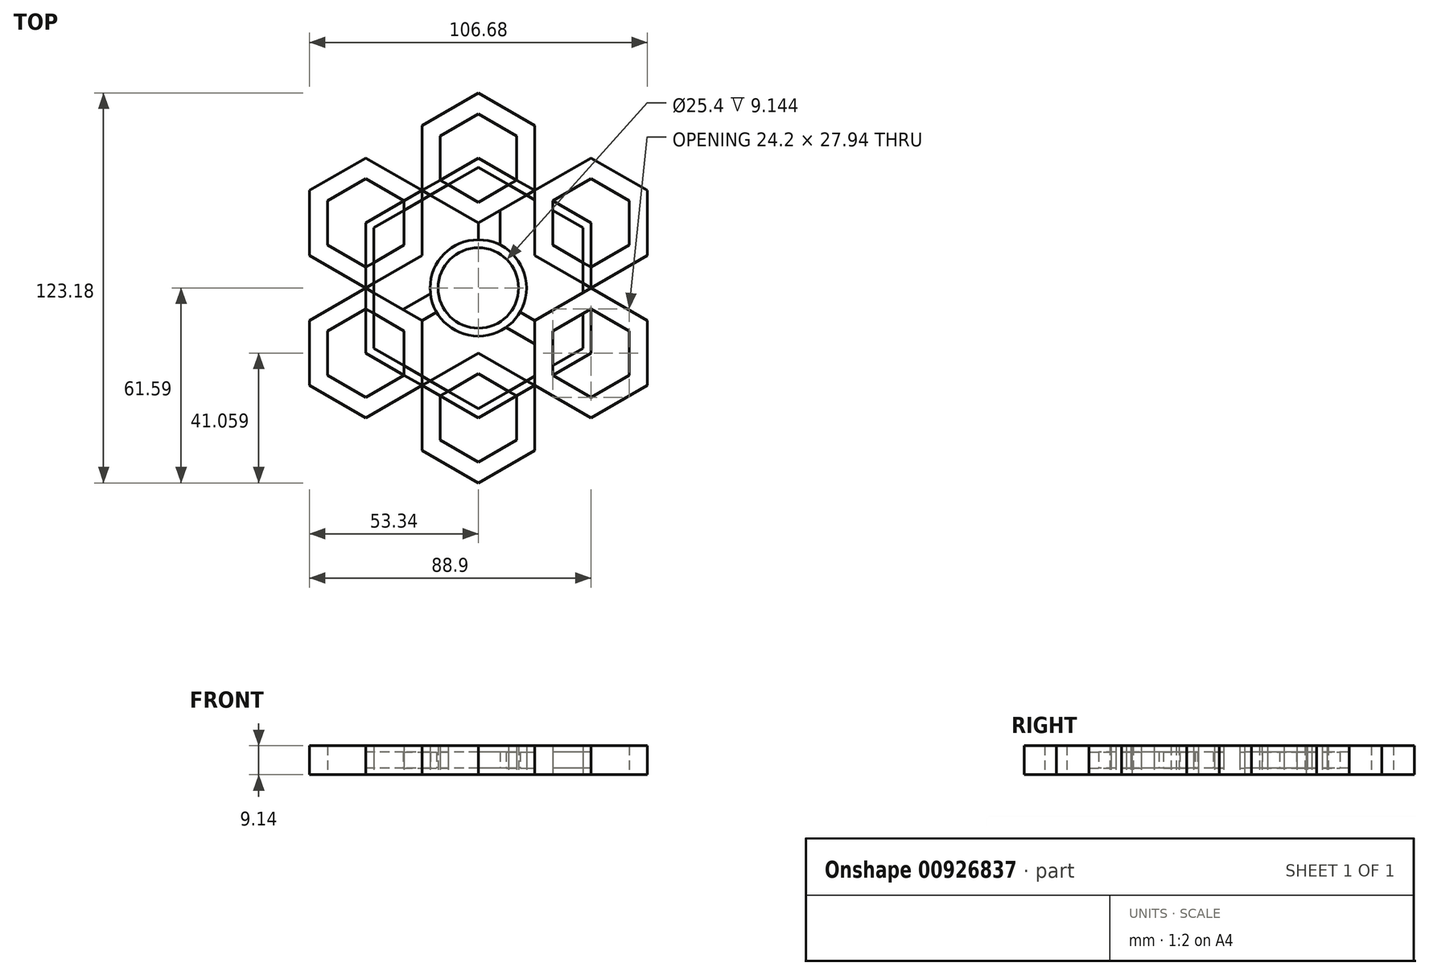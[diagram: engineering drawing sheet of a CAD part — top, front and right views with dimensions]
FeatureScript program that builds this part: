
annotation { "Feature Type Name" : "Feature", "Feature Type Description" : "" }
export const myFeature = defineFeature(function(context is Context, id is Id, definition is map)
    precondition{}
    {
        {
            var Q0;
            Q0=qCreatedBy(makeId("Top.planeOp"),FACE);
            var sketch = newSketch(context, id + "F0", { "sketchPlane" : qUnion([Q0])});
            skCircle(sketch, "E0", {"center": v(0, 0) * mm, "radius": 12.7 * mm});
            skCircle(sketch, "E1.cCircle", {"center": v(0, 0) * mm, "radius": 35.56 * mm, "construction": true});
            skLineSegment(sketch, "E1.0", {"start": v(35.56, 20.53) * mm, "end": v(35.56, -20.53) * mm});
            skLineSegment(sketch, "E1.1", {"start": v(35.56, -20.53) * mm, "end": v(0, -41.06) * mm});
            skLineSegment(sketch, "E1.2", {"start": v(0, -41.06) * mm, "end": v(-35.56, -20.53) * mm});
            skLineSegment(sketch, "E1.3", {"start": v(-35.56, -20.53) * mm, "end": v(-35.56, 20.53) * mm});
            skLineSegment(sketch, "E1.4", {"start": v(-35.56, 20.53) * mm, "end": v(0, 41.06) * mm});
            skLineSegment(sketch, "E1.5", {"start": v(0, 41.06) * mm, "end": v(35.56, 20.53) * mm});
            skPoint(sketch, "E1.0.midPoint", {"position": v(35.56, 0) * mm});
            skCircle(sketch, "E2.cCircle", {"center": v(35.56, 20.53) * mm, "radius": 20.53 * mm, "construction": true});
            skLineSegment(sketch, "E2.0", {"start": v(35.56, 0) * mm, "end": v(17.78, 10.27) * mm});
            skLineSegment(sketch, "E2.1", {"start": v(17.78, 10.27) * mm, "end": v(17.78, 30.8) * mm});
            skLineSegment(sketch, "E2.2", {"start": v(17.78, 30.8) * mm, "end": v(35.56, 41.06) * mm});
            skLineSegment(sketch, "E2.3", {"start": v(35.56, 41.06) * mm, "end": v(53.34, 30.8) * mm});
            skLineSegment(sketch, "E2.4", {"start": v(53.34, 30.8) * mm, "end": v(53.34, 10.27) * mm});
            skLineSegment(sketch, "E2.5", {"start": v(53.34, 10.27) * mm, "end": v(35.56, 0) * mm});
            skCircle(sketch, "E3.cCircle", {"center": v(0, 41.06) * mm, "radius": 20.53 * mm, "construction": true});
            skLineSegment(sketch, "E3.0", {"start": v(17.78, 30.8) * mm, "end": v(0, 20.53) * mm});
            skLineSegment(sketch, "E3.1", {"start": v(0, 20.53) * mm, "end": v(-17.78, 30.8) * mm});
            skLineSegment(sketch, "E3.2", {"start": v(-17.78, 30.8) * mm, "end": v(-17.78, 51.33) * mm});
            skLineSegment(sketch, "E3.3", {"start": v(-17.78, 51.33) * mm, "end": v(0, 61.6) * mm});
            skLineSegment(sketch, "E3.4", {"start": v(0, 61.6) * mm, "end": v(17.78, 51.33) * mm});
            skLineSegment(sketch, "E3.5", {"start": v(17.78, 51.33) * mm, "end": v(17.78, 30.8) * mm});
            skCircle(sketch, "E4.cCircle", {"center": v(-35.56, 20.53) * mm, "radius": 20.53 * mm, "construction": true});
            skLineSegment(sketch, "E4.0", {"start": v(-17.78, 30.8) * mm, "end": v(-17.78, 10.27) * mm});
            skLineSegment(sketch, "E4.1", {"start": v(-17.78, 10.27) * mm, "end": v(-35.56, 0) * mm});
            skLineSegment(sketch, "E4.2", {"start": v(-35.56, 0) * mm, "end": v(-53.34, 10.27) * mm});
            skLineSegment(sketch, "E4.3", {"start": v(-53.34, 10.27) * mm, "end": v(-53.34, 30.8) * mm});
            skLineSegment(sketch, "E4.4", {"start": v(-53.34, 30.8) * mm, "end": v(-35.56, 41.06) * mm});
            skLineSegment(sketch, "E4.5", {"start": v(-35.56, 41.06) * mm, "end": v(-17.78, 30.8) * mm});
            skCircle(sketch, "E5.cCircle", {"center": v(-35.56, -20.53) * mm, "radius": 20.53 * mm, "construction": true});
            skLineSegment(sketch, "E5.0", {"start": v(-35.56, 0) * mm, "end": v(-17.78, -10.27) * mm});
            skLineSegment(sketch, "E5.1", {"start": v(-17.78, -10.27) * mm, "end": v(-17.78, -30.8) * mm});
            skLineSegment(sketch, "E5.2", {"start": v(-17.78, -30.8) * mm, "end": v(-35.56, -41.06) * mm});
            skLineSegment(sketch, "E5.3", {"start": v(-35.56, -41.06) * mm, "end": v(-53.34, -30.8) * mm});
            skLineSegment(sketch, "E5.4", {"start": v(-53.34, -30.8) * mm, "end": v(-53.34, -10.27) * mm});
            skLineSegment(sketch, "E5.5", {"start": v(-53.34, -10.27) * mm, "end": v(-35.56, 0) * mm});
            skCircle(sketch, "E6.cCircle", {"center": v(0, -41.06) * mm, "radius": 20.53 * mm, "construction": true});
            skLineSegment(sketch, "E6.0", {"start": v(-17.78, -30.8) * mm, "end": v(0, -20.53) * mm});
            skLineSegment(sketch, "E6.1", {"start": v(0, -20.53) * mm, "end": v(17.78, -30.8) * mm});
            skLineSegment(sketch, "E6.2", {"start": v(17.78, -30.8) * mm, "end": v(17.78, -51.33) * mm});
            skLineSegment(sketch, "E6.3", {"start": v(17.78, -51.33) * mm, "end": v(0, -61.6) * mm});
            skLineSegment(sketch, "E6.4", {"start": v(0, -61.6) * mm, "end": v(-17.78, -51.33) * mm});
            skLineSegment(sketch, "E6.5", {"start": v(-17.78, -51.33) * mm, "end": v(-17.78, -30.8) * mm});
            skCircle(sketch, "E7.cCircle", {"center": v(35.56, -20.53) * mm, "radius": 20.53 * mm, "construction": true});
            skLineSegment(sketch, "E7.0", {"start": v(35.56, 0) * mm, "end": v(53.34, -10.27) * mm});
            skLineSegment(sketch, "E7.1", {"start": v(53.34, -10.27) * mm, "end": v(53.34, -30.8) * mm});
            skLineSegment(sketch, "E7.2", {"start": v(53.34, -30.8) * mm, "end": v(35.56, -41.06) * mm});
            skLineSegment(sketch, "E7.3", {"start": v(35.56, -41.06) * mm, "end": v(17.78, -30.8) * mm});
            skLineSegment(sketch, "E7.4", {"start": v(17.78, -30.8) * mm, "end": v(17.78, -10.27) * mm});
            skLineSegment(sketch, "E7.5", {"start": v(17.78, -10.27) * mm, "end": v(35.56, 0) * mm});
            skCircle(sketch, "E8.cCircle", {"center": v(-35.56, 20.53) * mm, "radius": 13.97 * mm, "construction": true});
            skLineSegment(sketch, "E8.0", {"start": v(-35.56, 6.56) * mm, "end": v(-47.66, 13.55) * mm});
            skLineSegment(sketch, "E8.1", {"start": v(-47.66, 13.55) * mm, "end": v(-47.66, 27.52) * mm});
            skLineSegment(sketch, "E8.2", {"start": v(-47.66, 27.52) * mm, "end": v(-35.56, 34.5) * mm});
            skLineSegment(sketch, "E8.3", {"start": v(-35.56, 34.5) * mm, "end": v(-23.46, 27.52) * mm});
            skLineSegment(sketch, "E8.4", {"start": v(-23.46, 27.52) * mm, "end": v(-23.46, 13.55) * mm});
            skLineSegment(sketch, "E8.5", {"start": v(-23.46, 13.55) * mm, "end": v(-35.56, 6.56) * mm});
            skCircle(sketch, "E9.cCircle", {"center": v(0, 41.06) * mm, "radius": 13.97 * mm, "construction": true});
            skLineSegment(sketch, "E9.0", {"start": v(0, 55.03) * mm, "end": v(12.1, 48.05) * mm});
            skLineSegment(sketch, "E9.1", {"start": v(12.1, 48.05) * mm, "end": v(12.1, 34.08) * mm});
            skLineSegment(sketch, "E9.2", {"start": v(12.1, 34.08) * mm, "end": v(0, 27.1) * mm});
            skLineSegment(sketch, "E9.3", {"start": v(0, 27.1) * mm, "end": v(-12.1, 34.08) * mm});
            skLineSegment(sketch, "E9.4", {"start": v(-12.1, 34.08) * mm, "end": v(-12.1, 48.05) * mm});
            skLineSegment(sketch, "E9.5", {"start": v(-12.1, 48.05) * mm, "end": v(0, 55.03) * mm});
            skCircle(sketch, "E10.cCircle", {"center": v(35.56, 20.53) * mm, "radius": 13.97 * mm, "construction": true});
            skLineSegment(sketch, "E10.0", {"start": v(35.56, 6.56) * mm, "end": v(23.46, 13.55) * mm});
            skLineSegment(sketch, "E10.1", {"start": v(23.46, 13.55) * mm, "end": v(23.46, 27.52) * mm});
            skLineSegment(sketch, "E10.2", {"start": v(23.46, 27.52) * mm, "end": v(35.56, 34.5) * mm});
            skLineSegment(sketch, "E10.3", {"start": v(35.56, 34.5) * mm, "end": v(47.66, 27.52) * mm});
            skLineSegment(sketch, "E10.4", {"start": v(47.66, 27.52) * mm, "end": v(47.66, 13.55) * mm});
            skLineSegment(sketch, "E10.5", {"start": v(47.66, 13.55) * mm, "end": v(35.56, 6.56) * mm});
            skCircle(sketch, "E11.cCircle", {"center": v(35.56, -20.53) * mm, "radius": 13.97 * mm, "construction": true});
            skLineSegment(sketch, "E11.0", {"start": v(35.56, -34.5) * mm, "end": v(23.46, -27.52) * mm});
            skLineSegment(sketch, "E11.1", {"start": v(23.46, -27.52) * mm, "end": v(23.46, -13.55) * mm});
            skLineSegment(sketch, "E11.2", {"start": v(23.46, -13.55) * mm, "end": v(35.56, -6.56) * mm});
            skLineSegment(sketch, "E11.3", {"start": v(35.56, -6.56) * mm, "end": v(47.66, -13.55) * mm});
            skLineSegment(sketch, "E11.4", {"start": v(47.66, -13.55) * mm, "end": v(47.66, -27.52) * mm});
            skLineSegment(sketch, "E11.5", {"start": v(47.66, -27.52) * mm, "end": v(35.56, -34.5) * mm});
            skCircle(sketch, "E12.cCircle", {"center": v(0, -41.06) * mm, "radius": 12.1 * mm, "construction": true});
            skLineSegment(sketch, "E12.0", {"start": v(0, -55.03) * mm, "end": v(-12.1, -48.05) * mm});
            skLineSegment(sketch, "E12.1", {"start": v(-12.1, -48.05) * mm, "end": v(-12.1, -34.08) * mm});
            skLineSegment(sketch, "E12.2", {"start": v(-12.1, -34.08) * mm, "end": v(0, -27.1) * mm});
            skLineSegment(sketch, "E12.3", {"start": v(0, -27.1) * mm, "end": v(12.1, -34.08) * mm});
            skLineSegment(sketch, "E12.4", {"start": v(12.1, -34.08) * mm, "end": v(12.1, -48.05) * mm});
            skLineSegment(sketch, "E12.5", {"start": v(12.1, -48.05) * mm, "end": v(0, -55.03) * mm});
            skPoint(sketch, "E12.0.midPoint", {"position": v(-6.05, -51.54) * mm});
            skCircle(sketch, "E13.cCircle", {"center": v(-35.56, -20.53) * mm, "radius": 13.97 * mm, "construction": true});
            skLineSegment(sketch, "E13.0", {"start": v(-35.56, -6.56) * mm, "end": v(-23.46, -13.55) * mm});
            skLineSegment(sketch, "E13.1", {"start": v(-23.46, -13.55) * mm, "end": v(-23.46, -27.52) * mm});
            skLineSegment(sketch, "E13.2", {"start": v(-23.46, -27.52) * mm, "end": v(-35.56, -34.5) * mm});
            skLineSegment(sketch, "E13.3", {"start": v(-35.56, -34.5) * mm, "end": v(-47.66, -27.52) * mm});
            skLineSegment(sketch, "E13.4", {"start": v(-47.66, -27.52) * mm, "end": v(-47.66, -13.55) * mm});
            skLineSegment(sketch, "E13.5", {"start": v(-47.66, -13.55) * mm, "end": v(-35.56, -6.56) * mm});
            skLineSegment(sketch, "E14", {"start": v(-17.78, -10.27) * mm, "end": v(0, 0) * mm});
            skLineSegment(sketch, "E15", {"start": v(0, 20.53) * mm, "end": v(0, 0) * mm});
            skLineSegment(sketch, "E16", {"start": v(0, 0) * mm, "end": v(17.78, -10.27) * mm});
            skLineSegment(sketch, "E17", {"start": v(0, 0) * mm, "end": v(0, -7.37) * mm});
            skLineSegment(sketch, "E18", {"start": v(0, -7.37) * mm, "end": v(0, 0) * mm});
            skLineSegment(sketch, "E19", {"start": v(0, 0) * mm, "end": v(6.87, 3.97) * mm});
            skLineSegment(sketch, "E20", {"start": v(0, 0) * mm, "end": v(-6, 3.46) * mm});
            skLineSegment(sketch, "E21", {"start": v(-6, 3.46) * mm, "end": v(-23.77, -6.8) * mm});
            skLineSegment(sketch, "E22", {"start": v(6.87, 3.97) * mm, "end": v(6.87, 24.5) * mm});
            skLineSegment(sketch, "E23", {"start": v(0, -7.37) * mm, "end": v(17.78, -17.63) * mm});
            skCircle(sketch, "E24", {"center": v(0, 0) * mm, "radius": 15.24 * mm});
            skCircle(sketch, "E25.cCircle", {"center": v(0, 0) * mm, "radius": 38.1 * mm, "construction": true});
            skLineSegment(sketch, "E25.0", {"start": v(0, 38.1) * mm, "end": v(33, 19.05) * mm});
            skLineSegment(sketch, "E25.1", {"start": v(33, 19.05) * mm, "end": v(33, -19.05) * mm});
            skLineSegment(sketch, "E25.2", {"start": v(33, -19.05) * mm, "end": v(0, -38.1) * mm});
            skLineSegment(sketch, "E25.3", {"start": v(0, -38.1) * mm, "end": v(-33, -19.05) * mm});
            skLineSegment(sketch, "E25.4", {"start": v(-33, -19.05) * mm, "end": v(-33, 19.05) * mm});
            skLineSegment(sketch, "E25.5", {"start": v(-33, 19.05) * mm, "end": v(0, 38.1) * mm});
            skSolve(sketch);
        }
        {
            var Q0;
            {var subQ0=sQuery(id+"F0.wireOp",EDGE,"E4.2");Q0=makeQuery(id+"F0.imprint","IMPRINT",FACE,{"disambiguationData":[TD([[makeQuery(id+"F0.imprint","IMPRINT",EDGE,{"derivedFrom":subQ0}),-1.0]])]});}
            var Q1;
            {var subQ0=sQuery(id+"F0.wireOp",EDGE,"E3.2");Q1=makeQuery(id+"F0.imprint","IMPRINT",FACE,{"disambiguationData":[TD([[makeQuery(id+"F0.imprint","IMPRINT",EDGE,{"derivedFrom":subQ0}),-1.0]])]});}
            var Q2;
            {var subQ1=sQuery(id+"F0.wireOp",EDGE,"E2.2");Q2=makeQuery(id+"F0.imprint","IMPRINT",FACE,{"disambiguationData":[TD([[makeQuery(id+"F0.imprint","IMPRINT",EDGE,{"derivedFrom":subQ1}),-1.0]])]});}
            var Q3;
            {var subQ0=sQuery(id+"F0.wireOp",EDGE,"E7.0");Q3=makeQuery(id+"F0.imprint","IMPRINT",FACE,{"disambiguationData":[TD([[makeQuery(id+"F0.imprint","IMPRINT",EDGE,{"derivedFrom":subQ0}),-1.0]])]});}
            var Q4;
            {var subQ0=sQuery(id+"F0.wireOp",EDGE,"E6.2");Q4=makeQuery(id+"F0.imprint","IMPRINT",FACE,{"disambiguationData":[TD([[makeQuery(id+"F0.imprint","IMPRINT",EDGE,{"derivedFrom":subQ0}),-1.0]])]});}
            var Q5;
            {var subQ0=sQuery(id+"F0.wireOp",EDGE,"E5.2");Q5=makeQuery(id+"F0.imprint","IMPRINT",FACE,{"disambiguationData":[TD([[makeQuery(id+"F0.imprint","IMPRINT",EDGE,{"derivedFrom":subQ0}),-1.0]])]});}
            var Q6;
            {var subQ7=sQuery(id+"F0.wireOp",EDGE,"E4.1");var subQ8=sQuery(id+"F0.wireOp",EDGE,"E4.0");var subQ9=makeQuery(id+"F0.imprint","INTERSECT",VERTEX,{"derivedFrom":[subQ8,subQ7]});Q6=makeQuery(id+"F0.imprint","IMPRINT",FACE,{"disambiguationData":[TD([[makeQuery(id+"F0.imprint","IMPRINT",EDGE,{"disambiguationData":[TD([[subQ9,1.0]])],"derivedFrom":subQ8}),-1.0]])]});}
            var Q7;
            {var subQ6=sQuery(id+"F0.wireOp",EDGE,"E3.0");var subQ11=makeQuery(id+"F0.imprint","INTERSECT",VERTEX,{"derivedFrom":[subQ6,sQuery(id+"F0.wireOp",EDGE,"E22")]});Q7=makeQuery(id+"F0.imprint","IMPRINT",FACE,{"disambiguationData":[TD([[makeQuery(id+"F0.imprint","IMPRINT",EDGE,{"disambiguationData":[TD([[subQ11,1.0]])],"derivedFrom":subQ6}),-1.0]])]});}
            var Q8;
            {var subQ7=sQuery(id+"F0.wireOp",EDGE,"E2.1");var subQ8=sQuery(id+"F0.wireOp",EDGE,"E2.0");var subQ9=makeQuery(id+"F0.imprint","INTERSECT",VERTEX,{"derivedFrom":[subQ8,subQ7]});Q8=makeQuery(id+"F0.imprint","IMPRINT",FACE,{"disambiguationData":[TD([[makeQuery(id+"F0.imprint","IMPRINT",EDGE,{"disambiguationData":[TD([[subQ9,1.0]])],"derivedFrom":subQ8}),-1.0]])]});}
            var Q9;
            {var subQ1=sQuery(id+"F0.wireOp",EDGE,"E7.4");var subQ9=makeQuery(id+"F0.imprint","INTERSECT",VERTEX,{"derivedFrom":[subQ1,sQuery(id+"F0.wireOp",EDGE,"E23")]});Q9=makeQuery(id+"F0.imprint","IMPRINT",FACE,{"disambiguationData":[TD([[makeQuery(id+"F0.imprint","IMPRINT",EDGE,{"disambiguationData":[TD([[subQ9,1.0]])],"derivedFrom":subQ1}),-1.0]])]});}
            var Q10;
            {var subQ6=sQuery(id+"F0.wireOp",EDGE,"E6.0");var subQ9=sQuery(id+"F0.wireOp",EDGE,"E6.1");var subQ10=makeQuery(id+"F0.imprint","INTERSECT",VERTEX,{"derivedFrom":[subQ6,subQ9]});Q10=makeQuery(id+"F0.imprint","IMPRINT",FACE,{"disambiguationData":[TD([[makeQuery(id+"F0.imprint","IMPRINT",EDGE,{"disambiguationData":[TD([[subQ10,1.0]])],"derivedFrom":subQ6}),-1.0]])]});}
            var Q11;
            {var subQ1=sQuery(id+"F0.wireOp",EDGE,"E5.0");var subQ10=makeQuery(id+"F0.imprint","INTERSECT",VERTEX,{"derivedFrom":[subQ1,sQuery(id+"F0.wireOp",EDGE,"E21")]});Q11=makeQuery(id+"F0.imprint","IMPRINT",FACE,{"disambiguationData":[TD([[makeQuery(id+"F0.imprint","IMPRINT",EDGE,{"disambiguationData":[TD([[subQ10,1.0]])],"derivedFrom":subQ1}),-1.0]])]});}
            var Q12;
            {var subQ0=sQuery(id+"F0.wireOp",EDGE,"E14");var subQ1=sQuery(id+"F0.wireOp",EDGE,"E0");var subQ2=makeQuery(id+"F0.imprint","INTERSECT",VERTEX,{"derivedFrom":[subQ1,subQ0]});Q12=makeQuery(id+"F0.imprint","IMPRINT",FACE,{"disambiguationData":[TD([[makeQuery(id+"F0.imprint","IMPRINT",EDGE,{"disambiguationData":[TD([[subQ2,-1.0]])],"derivedFrom":subQ1}),-1.0]])]});}
            var Q13;
            {var subQ0=sQuery(id+"F0.wireOp",EDGE,"E15");var subQ1=sQuery(id+"F0.wireOp",EDGE,"E0");var subQ2=makeQuery(id+"F0.imprint","INTERSECT",VERTEX,{"derivedFrom":[subQ1,subQ0]});Q13=makeQuery(id+"F0.imprint","IMPRINT",FACE,{"disambiguationData":[TD([[makeQuery(id+"F0.imprint","IMPRINT",EDGE,{"disambiguationData":[TD([[subQ2,-1.0]])],"derivedFrom":subQ1}),-1.0]])]});}
            var Q14;
            {var subQ0=sQuery(id+"F0.wireOp",EDGE,"E22");var subQ1=sQuery(id+"F0.wireOp",EDGE,"E0");var subQ2=makeQuery(id+"F0.imprint","INTERSECT",VERTEX,{"derivedFrom":[subQ1,subQ0]});Q14=makeQuery(id+"F0.imprint","IMPRINT",FACE,{"disambiguationData":[TD([[makeQuery(id+"F0.imprint","IMPRINT",EDGE,{"disambiguationData":[TD([[subQ2,1.0]])],"derivedFrom":subQ1}),-1.0]])]});}
            var Q15;
            {var subQ0=sQuery(id+"F0.wireOp",EDGE,"E23");var subQ1=sQuery(id+"F0.wireOp",EDGE,"E0");var subQ2=makeQuery(id+"F0.imprint","INTERSECT",VERTEX,{"derivedFrom":[subQ1,subQ0]});Q15=makeQuery(id+"F0.imprint","IMPRINT",FACE,{"disambiguationData":[TD([[makeQuery(id+"F0.imprint","IMPRINT",EDGE,{"disambiguationData":[TD([[subQ2,-1.0]])],"derivedFrom":subQ1}),-1.0]])]});}
            var Q16;
            {var subQ0=sQuery(id+"F0.wireOp",EDGE,"E15");var subQ1=sQuery(id+"F0.wireOp",EDGE,"E0");var subQ2=makeQuery(id+"F0.imprint","INTERSECT",VERTEX,{"derivedFrom":[subQ1,subQ0]});Q16=makeQuery(id+"F0.imprint","IMPRINT",FACE,{"disambiguationData":[TD([[makeQuery(id+"F0.imprint","IMPRINT",EDGE,{"disambiguationData":[TD([[subQ2,1.0]])],"derivedFrom":subQ1}),-1.0]])]});}
            var Q17;
            {var subQ0=sQuery(id+"F0.wireOp",EDGE,"E21");var subQ1=sQuery(id+"F0.wireOp",EDGE,"E0");var subQ2=makeQuery(id+"F0.imprint","INTERSECT",VERTEX,{"derivedFrom":[subQ1,subQ0]});Q17=makeQuery(id+"F0.imprint","IMPRINT",FACE,{"disambiguationData":[TD([[makeQuery(id+"F0.imprint","IMPRINT",EDGE,{"disambiguationData":[TD([[subQ2,-1.0]])],"derivedFrom":subQ1}),-1.0]])]});}
            extrude(context, id + "F1", {"entities" : qUnion([Q0, Q1, Q2, Q3, Q4, Q5, Q6, Q7, Q8, Q9, Q10, Q11, Q12, Q13, Q14, Q15, Q16, Q17]), "depth" : 4.57 * mm, "offsetDistance" : 25.4 * mm, "hasSecondDirection" : true, "secondDirectionOppositeDirection" : true, "secondDirectionDepth" : 4.57 * mm});
        }
        {
            var Q0;
            {var subQ1=sQuery(id+"F0.wireOp",EDGE,"E5.0");var subQ3=sQuery(id+"F0.wireOp",EDGE,"E21");var subQ4=makeQuery(id+"F0.imprint","INTERSECT",VERTEX,{"derivedFrom":[subQ1,subQ3]});Q0=makeQuery(id+"F0.imprint","IMPRINT",FACE,{"disambiguationData":[TD([[makeQuery(id+"F0.imprint","IMPRINT",EDGE,{"disambiguationData":[TD([[subQ4,1.0]])],"derivedFrom":subQ3}),1.0]])]});}
            var Q1;
            {var subQ3=sQuery(id+"F0.wireOp",EDGE,"E25.4");var subQ9=sQuery(id+"F0.wireOp",EDGE,"E25.5");var subQ11=makeQuery(id+"F0.imprint","INTERSECT",VERTEX,{"derivedFrom":[subQ3,subQ9]});Q1=makeQuery(id+"F0.imprint","IMPRINT",FACE,{"disambiguationData":[TD([[makeQuery(id+"F0.imprint","IMPRINT",EDGE,{"disambiguationData":[TD([[subQ11,1.0]])],"derivedFrom":subQ3}),1.0]])]});}
            var Q2;
            {var subQ1=sQuery(id+"F0.wireOp",EDGE,"E3.1");var subQ3=sQuery(id+"F0.wireOp",EDGE,"E25.5");var subQ4=makeQuery(id+"F0.imprint","INTERSECT",VERTEX,{"derivedFrom":[subQ1,subQ3]});Q2=makeQuery(id+"F0.imprint","IMPRINT",FACE,{"disambiguationData":[TD([[makeQuery(id+"F0.imprint","IMPRINT",EDGE,{"disambiguationData":[TD([[subQ4,1.0]])],"derivedFrom":subQ3}),1.0]])]});}
            var Q3;
            {var subQ3=sQuery(id+"F0.wireOp",EDGE,"E25.5");var subQ8=sQuery(id+"F0.wireOp",EDGE,"E25.0");var subQ11=makeQuery(id+"F0.imprint","INTERSECT",VERTEX,{"derivedFrom":[subQ8,subQ3]});Q3=makeQuery(id+"F0.imprint","IMPRINT",FACE,{"disambiguationData":[TD([[makeQuery(id+"F0.imprint","IMPRINT",EDGE,{"disambiguationData":[TD([[subQ11,-1.0]])],"derivedFrom":subQ8}),1.0]])]});}
            var Q4;
            {var subQ1=sQuery(id+"F0.wireOp",EDGE,"E2.1");var subQ3=sQuery(id+"F0.wireOp",EDGE,"E25.0");var subQ4=makeQuery(id+"F0.imprint","INTERSECT",VERTEX,{"derivedFrom":[subQ1,subQ3]});Q4=makeQuery(id+"F0.imprint","IMPRINT",FACE,{"disambiguationData":[TD([[makeQuery(id+"F0.imprint","IMPRINT",EDGE,{"disambiguationData":[TD([[subQ4,1.0]])],"derivedFrom":subQ3}),1.0]])]});}
            var Q5;
            {var subQ1=sQuery(id+"F0.wireOp",EDGE,"E2.0");var subQ3=sQuery(id+"F0.wireOp",EDGE,"E25.1");var subQ4=makeQuery(id+"F0.imprint","INTERSECT",VERTEX,{"derivedFrom":[subQ1,subQ3]});Q5=makeQuery(id+"F0.imprint","IMPRINT",FACE,{"disambiguationData":[TD([[makeQuery(id+"F0.imprint","IMPRINT",EDGE,{"disambiguationData":[TD([[subQ4,-1.0]])],"derivedFrom":subQ3}),1.0]])]});}
            var Q6;
            {var subQ1=sQuery(id+"F0.wireOp",EDGE,"E6.1");var subQ3=sQuery(id+"F0.wireOp",EDGE,"E25.2");var subQ4=makeQuery(id+"F0.imprint","INTERSECT",VERTEX,{"derivedFrom":[subQ1,subQ3]});Q6=makeQuery(id+"F0.imprint","IMPRINT",FACE,{"disambiguationData":[TD([[makeQuery(id+"F0.imprint","IMPRINT",EDGE,{"disambiguationData":[TD([[subQ4,1.0]])],"derivedFrom":subQ3}),1.0]])]});}
            var Q7;
            {var subQ1=sQuery(id+"F0.wireOp",EDGE,"E5.1");var subQ3=sQuery(id+"F0.wireOp",EDGE,"E25.3");var subQ4=makeQuery(id+"F0.imprint","INTERSECT",VERTEX,{"derivedFrom":[subQ1,subQ3]});Q7=makeQuery(id+"F0.imprint","IMPRINT",FACE,{"disambiguationData":[TD([[makeQuery(id+"F0.imprint","IMPRINT",EDGE,{"disambiguationData":[TD([[subQ4,1.0]])],"derivedFrom":subQ3}),1.0]])]});}
            var Q8;
            {var subQ3=sQuery(id+"F0.wireOp",EDGE,"E25.3");var subQ8=sQuery(id+"F0.wireOp",EDGE,"E25.4");var subQ10=makeQuery(id+"F0.imprint","INTERSECT",VERTEX,{"derivedFrom":[subQ3,subQ8]});Q8=makeQuery(id+"F0.imprint","IMPRINT",FACE,{"disambiguationData":[TD([[makeQuery(id+"F0.imprint","IMPRINT",EDGE,{"disambiguationData":[TD([[subQ10,1.0]])],"derivedFrom":subQ3}),1.0]])]});}
            var Q9;
            {var subQ3=sQuery(id+"F0.wireOp",EDGE,"E25.3");var subQ5=sQuery(id+"F0.wireOp",EDGE,"E25.2");var subQ6=makeQuery(id+"F0.imprint","INTERSECT",VERTEX,{"derivedFrom":[subQ5,subQ3]});Q9=makeQuery(id+"F0.imprint","IMPRINT",FACE,{"disambiguationData":[TD([[makeQuery(id+"F0.imprint","IMPRINT",EDGE,{"disambiguationData":[TD([[subQ6,1.0]])],"derivedFrom":subQ5}),1.0]])]});}
            var Q10;
            {var subQ3=sQuery(id+"F0.wireOp",EDGE,"E25.2");var subQ9=sQuery(id+"F0.wireOp",EDGE,"E25.1");var subQ11=makeQuery(id+"F0.imprint","INTERSECT",VERTEX,{"derivedFrom":[subQ9,subQ3]});Q10=makeQuery(id+"F0.imprint","IMPRINT",FACE,{"disambiguationData":[TD([[makeQuery(id+"F0.imprint","IMPRINT",EDGE,{"disambiguationData":[TD([[subQ11,1.0]])],"derivedFrom":subQ9}),1.0]])]});}
            var Q11;
            {var subQ3=sQuery(id+"F0.wireOp",EDGE,"E25.0");var subQ8=sQuery(id+"F0.wireOp",EDGE,"E25.1");var subQ11=makeQuery(id+"F0.imprint","INTERSECT",VERTEX,{"derivedFrom":[subQ3,subQ8]});Q11=makeQuery(id+"F0.imprint","IMPRINT",FACE,{"disambiguationData":[TD([[makeQuery(id+"F0.imprint","IMPRINT",EDGE,{"disambiguationData":[TD([[subQ11,1.0]])],"derivedFrom":subQ3}),1.0]])]});}
            var Q12;
            {var subQ1=sQuery(id+"F0.wireOp",EDGE,"E7.4");var subQ3=sQuery(id+"F0.wireOp",EDGE,"E23");var subQ4=makeQuery(id+"F0.imprint","INTERSECT",VERTEX,{"derivedFrom":[subQ1,subQ3]});Q12=makeQuery(id+"F0.imprint","IMPRINT",FACE,{"disambiguationData":[TD([[makeQuery(id+"F0.imprint","IMPRINT",EDGE,{"disambiguationData":[TD([[subQ4,1.0]])],"derivedFrom":subQ3}),1.0]])]});}
            var Q13;
            {var subQ1=sQuery(id+"F0.wireOp",EDGE,"E3.0");var subQ3=sQuery(id+"F0.wireOp",EDGE,"E22");var subQ4=makeQuery(id+"F0.imprint","INTERSECT",VERTEX,{"derivedFrom":[subQ1,subQ3]});Q13=makeQuery(id+"F0.imprint","IMPRINT",FACE,{"disambiguationData":[TD([[makeQuery(id+"F0.imprint","IMPRINT",EDGE,{"disambiguationData":[TD([[subQ4,1.0]])],"derivedFrom":subQ3}),1.0]])]});}
            extrude(context, id + "F2", {"entities" : qUnion([Q0, Q1, Q2, Q3, Q4, Q5, Q6, Q7, Q8, Q9, Q10, Q11, Q12, Q13]), "depth" : 2.54 * mm, "offsetDistance" : 25.4 * mm, "hasSecondDirection" : true, "secondDirectionOppositeDirection" : true, "secondDirectionDepth" : 2.54 * mm});
        }
        {
            var Q0;
            {var subQ0=sQuery(id+"F0.wireOp",EDGE,"E6.1");var subQ5=sQuery(id+"F0.wireOp",EDGE,"E25.2");var subQ6=makeQuery(id+"F0.imprint","INTERSECT",VERTEX,{"derivedFrom":[subQ0,subQ5]});Q0=makeQuery(id+"F0.imprint","IMPRINT",FACE,{"disambiguationData":[TD([[makeQuery(id+"F0.imprint","IMPRINT",EDGE,{"disambiguationData":[TD([[subQ6,-1.0]])],"derivedFrom":subQ5}),1.0]])]});}
            var Q1;
            {var subQ0=sQuery(id+"F0.wireOp",EDGE,"E6.0");var subQ5=sQuery(id+"F0.wireOp",EDGE,"E25.3");var subQ7=makeQuery(id+"F0.imprint","INTERSECT",VERTEX,{"derivedFrom":[subQ0,subQ5]});Q1=makeQuery(id+"F0.imprint","IMPRINT",FACE,{"disambiguationData":[TD([[makeQuery(id+"F0.imprint","IMPRINT",EDGE,{"disambiguationData":[TD([[subQ7,1.0]])],"derivedFrom":subQ5}),1.0]])]});}
            var Q2;
            {var subQ0=sQuery(id+"F0.wireOp",EDGE,"E5.1");var subQ5=sQuery(id+"F0.wireOp",EDGE,"E25.3");var subQ6=makeQuery(id+"F0.imprint","INTERSECT",VERTEX,{"derivedFrom":[subQ0,subQ5]});Q2=makeQuery(id+"F0.imprint","IMPRINT",FACE,{"disambiguationData":[TD([[makeQuery(id+"F0.imprint","IMPRINT",EDGE,{"disambiguationData":[TD([[subQ6,-1.0]])],"derivedFrom":subQ5}),1.0]])]});}
            var Q3;
            {var subQ0=sQuery(id+"F0.wireOp",EDGE,"E5.0");var subQ5=sQuery(id+"F0.wireOp",EDGE,"E25.4");var subQ6=makeQuery(id+"F0.imprint","INTERSECT",VERTEX,{"derivedFrom":[subQ0,subQ5]});Q3=makeQuery(id+"F0.imprint","IMPRINT",FACE,{"disambiguationData":[TD([[makeQuery(id+"F0.imprint","IMPRINT",EDGE,{"disambiguationData":[TD([[subQ6,1.0]])],"derivedFrom":subQ5}),1.0]])]});}
            var Q4;
            {var subQ0=sQuery(id+"F0.wireOp",EDGE,"E4.1");var subQ5=sQuery(id+"F0.wireOp",EDGE,"E25.4");var subQ6=makeQuery(id+"F0.imprint","INTERSECT",VERTEX,{"derivedFrom":[subQ0,subQ5]});Q4=makeQuery(id+"F0.imprint","IMPRINT",FACE,{"disambiguationData":[TD([[makeQuery(id+"F0.imprint","IMPRINT",EDGE,{"disambiguationData":[TD([[subQ6,-1.0]])],"derivedFrom":subQ5}),1.0]])]});}
            var Q5;
            {var subQ0=sQuery(id+"F0.wireOp",EDGE,"E4.0");var subQ5=sQuery(id+"F0.wireOp",EDGE,"E25.5");var subQ6=makeQuery(id+"F0.imprint","INTERSECT",VERTEX,{"derivedFrom":[subQ0,subQ5]});Q5=makeQuery(id+"F0.imprint","IMPRINT",FACE,{"disambiguationData":[TD([[makeQuery(id+"F0.imprint","IMPRINT",EDGE,{"disambiguationData":[TD([[subQ6,1.0]])],"derivedFrom":subQ5}),1.0]])]});}
            var Q6;
            {var subQ0=sQuery(id+"F0.wireOp",EDGE,"E3.1");var subQ5=sQuery(id+"F0.wireOp",EDGE,"E25.5");var subQ7=makeQuery(id+"F0.imprint","INTERSECT",VERTEX,{"derivedFrom":[subQ0,subQ5]});Q6=makeQuery(id+"F0.imprint","IMPRINT",FACE,{"disambiguationData":[TD([[makeQuery(id+"F0.imprint","IMPRINT",EDGE,{"disambiguationData":[TD([[subQ7,-1.0]])],"derivedFrom":subQ5}),1.0]])]});}
            var Q7;
            {var subQ0=sQuery(id+"F0.wireOp",EDGE,"E3.0");var subQ5=sQuery(id+"F0.wireOp",EDGE,"E25.0");var subQ6=makeQuery(id+"F0.imprint","INTERSECT",VERTEX,{"derivedFrom":[subQ0,subQ5]});Q7=makeQuery(id+"F0.imprint","IMPRINT",FACE,{"disambiguationData":[TD([[makeQuery(id+"F0.imprint","IMPRINT",EDGE,{"disambiguationData":[TD([[subQ6,1.0]])],"derivedFrom":subQ5}),1.0]])]});}
            var Q8;
            {var subQ0=sQuery(id+"F0.wireOp",EDGE,"E2.0");var subQ5=sQuery(id+"F0.wireOp",EDGE,"E25.1");var subQ7=makeQuery(id+"F0.imprint","INTERSECT",VERTEX,{"derivedFrom":[subQ0,subQ5]});Q8=makeQuery(id+"F0.imprint","IMPRINT",FACE,{"disambiguationData":[TD([[makeQuery(id+"F0.imprint","IMPRINT",EDGE,{"disambiguationData":[TD([[subQ7,1.0]])],"derivedFrom":subQ5}),1.0]])]});}
            var Q9;
            {var subQ0=sQuery(id+"F0.wireOp",EDGE,"E7.4");var subQ5=sQuery(id+"F0.wireOp",EDGE,"E25.2");var subQ6=makeQuery(id+"F0.imprint","INTERSECT",VERTEX,{"derivedFrom":[subQ0,subQ5]});Q9=makeQuery(id+"F0.imprint","IMPRINT",FACE,{"disambiguationData":[TD([[makeQuery(id+"F0.imprint","IMPRINT",EDGE,{"disambiguationData":[TD([[subQ6,1.0]])],"derivedFrom":subQ5}),1.0]])]});}
            var Q10;
            {var subQ0=sQuery(id+"F0.wireOp",EDGE,"E7.5");var subQ5=sQuery(id+"F0.wireOp",EDGE,"E25.1");var subQ6=makeQuery(id+"F0.imprint","INTERSECT",VERTEX,{"derivedFrom":[subQ0,subQ5]});Q10=makeQuery(id+"F0.imprint","IMPRINT",FACE,{"disambiguationData":[TD([[makeQuery(id+"F0.imprint","IMPRINT",EDGE,{"disambiguationData":[TD([[subQ6,-1.0]])],"derivedFrom":subQ5}),1.0]])]});}
            var Q11;
            {var subQ0=sQuery(id+"F0.wireOp",EDGE,"E2.1");var subQ5=sQuery(id+"F0.wireOp",EDGE,"E25.0");var subQ6=makeQuery(id+"F0.imprint","INTERSECT",VERTEX,{"derivedFrom":[subQ0,subQ5]});Q11=makeQuery(id+"F0.imprint","IMPRINT",FACE,{"disambiguationData":[TD([[makeQuery(id+"F0.imprint","IMPRINT",EDGE,{"disambiguationData":[TD([[subQ6,-1.0]])],"derivedFrom":subQ5}),1.0]])]});}
            extrude(context, id + "F3", {"entities" : qUnion([Q0, Q1, Q2, Q3, Q4, Q5, Q6, Q7, Q8, Q9, Q10, Q11]), "depth" : 4.57 * mm, "offsetDistance" : 25.4 * mm, "hasSecondDirection" : true, "secondDirectionOppositeDirection" : true, "secondDirectionDepth" : 4.57 * mm});
        }
        {
            var Q0;
            {var subQ1=sQuery(id+"F0.wireOp",EDGE,"E4.1");var subQ3=sQuery(id+"F0.wireOp",EDGE,"E25.4");var subQ4=makeQuery(id+"F0.imprint","INTERSECT",VERTEX,{"derivedFrom":[subQ1,subQ3]});Q0=makeQuery(id+"F0.imprint","IMPRINT",FACE,{"disambiguationData":[TD([[makeQuery(id+"F0.imprint","IMPRINT",EDGE,{"disambiguationData":[TD([[subQ4,1.0]])],"derivedFrom":subQ3}),1.0]])]});}
            extrude(context, id + "F4", {"entities" : qUnion([Q0]), "depth" : 2.54 * mm, "offsetDistance" : 25.4 * mm, "hasSecondDirection" : true, "secondDirectionOppositeDirection" : true, "secondDirectionDepth" : 2.54 * mm});
        }
        {
            var Q0;
            Q0=makeQuery(id+"F2.opExtrude","SWEPT_BODY",BODY,{"disambiguationData":[OSD([sQuery(id+"F0.wireOp",EDGE,"E1.0"),sQuery(id+"F0.wireOp",EDGE,"E1.1"),sQuery(id+"F0.wireOp",EDGE,"E11.1"),sQuery(id+"F0.wireOp",EDGE,"E11.2"),sQuery(id+"F0.wireOp",EDGE,"E25.1"),sQuery(id+"F0.wireOp",EDGE,"E25.2")])]});
            var Q1;
            Q1=makeQuery(id+"F3.opExtrude","SWEPT_BODY",BODY,{"disambiguationData":[OSD([sQuery(id+"F0.wireOp",EDGE,"E1.0"),sQuery(id+"F0.wireOp",EDGE,"E7.5"),sQuery(id+"F0.wireOp",EDGE,"E11.2"),sQuery(id+"F0.wireOp",EDGE,"E25.1")])]});
            var Q2;
            Q2=makeQuery(id+"F1.opExtrude","SWEPT_BODY",BODY,{"disambiguationData":[OSD([sQuery(id+"F0.wireOp",EDGE,"E1.0"),sQuery(id+"F0.wireOp",EDGE,"E1.1"),sQuery(id+"F0.wireOp",EDGE,"E7.0"),sQuery(id+"F0.wireOp",EDGE,"E7.1"),sQuery(id+"F0.wireOp",EDGE,"E7.2"),sQuery(id+"F0.wireOp",EDGE,"E7.3"),sQuery(id+"F0.wireOp",EDGE,"E11.0"),sQuery(id+"F0.wireOp",EDGE,"E11.3"),sQuery(id+"F0.wireOp",EDGE,"E11.4"),sQuery(id+"F0.wireOp",EDGE,"E11.5")])]});
            var Q3;
            Q3=makeQuery(id+"F3.opExtrude","SWEPT_BODY",BODY,{"disambiguationData":[OSD([sQuery(id+"F0.wireOp",EDGE,"E1.1"),sQuery(id+"F0.wireOp",EDGE,"E7.4"),sQuery(id+"F0.wireOp",EDGE,"E11.1"),sQuery(id+"F0.wireOp",EDGE,"E25.2")])]});
            var Q4;
            Q4=makeQuery(id+"F2.opExtrude","SWEPT_BODY",BODY,{"disambiguationData":[OSD([sQuery(id+"F0.wireOp",EDGE,"E7.4"),sQuery(id+"F0.wireOp",EDGE,"E16"),sQuery(id+"F0.wireOp",EDGE,"E23"),sQuery(id+"F0.wireOp",EDGE,"E24")])]});
            var Q5;
            Q5=makeQuery(id+"F1.opExtrude","SWEPT_BODY",BODY,{"disambiguationData":[OSD([sQuery(id+"F0.wireOp",EDGE,"E7.4"),sQuery(id+"F0.wireOp",EDGE,"E7.5"),sQuery(id+"F0.wireOp",EDGE,"E11.1"),sQuery(id+"F0.wireOp",EDGE,"E11.2"),sQuery(id+"F0.wireOp",EDGE,"E25.1"),sQuery(id+"F0.wireOp",EDGE,"E25.2")])]});
            var Q6;
            Q6=makeQuery(id+"F1.opExtrude","SWEPT_BODY",BODY,{"disambiguationData":[OSD([sQuery(id+"F0.wireOp",EDGE,"E1.0"),sQuery(id+"F0.wireOp",EDGE,"E1.5"),sQuery(id+"F0.wireOp",EDGE,"E2.2"),sQuery(id+"F0.wireOp",EDGE,"E2.3"),sQuery(id+"F0.wireOp",EDGE,"E2.4"),sQuery(id+"F0.wireOp",EDGE,"E2.5"),sQuery(id+"F0.wireOp",EDGE,"E10.2"),sQuery(id+"F0.wireOp",EDGE,"E10.3"),sQuery(id+"F0.wireOp",EDGE,"E10.4"),sQuery(id+"F0.wireOp",EDGE,"E10.5")])]});
            var Q7;
            Q7=makeQuery(id+"F2.opExtrude","SWEPT_BODY",BODY,{"disambiguationData":[OSD([sQuery(id+"F0.wireOp",EDGE,"E1.0"),sQuery(id+"F0.wireOp",EDGE,"E1.5"),sQuery(id+"F0.wireOp",EDGE,"E10.0"),sQuery(id+"F0.wireOp",EDGE,"E10.1"),sQuery(id+"F0.wireOp",EDGE,"E25.0"),sQuery(id+"F0.wireOp",EDGE,"E25.1")])]});
            var Q8;
            Q8=makeQuery(id+"F1.opExtrude","SWEPT_BODY",BODY,{"disambiguationData":[OSD([sQuery(id+"F0.wireOp",EDGE,"E1.1"),sQuery(id+"F0.wireOp",EDGE,"E1.2"),sQuery(id+"F0.wireOp",EDGE,"E6.2"),sQuery(id+"F0.wireOp",EDGE,"E6.3"),sQuery(id+"F0.wireOp",EDGE,"E6.4"),sQuery(id+"F0.wireOp",EDGE,"E6.5"),sQuery(id+"F0.wireOp",EDGE,"E12.0"),sQuery(id+"F0.wireOp",EDGE,"E12.1"),sQuery(id+"F0.wireOp",EDGE,"E12.4"),sQuery(id+"F0.wireOp",EDGE,"E12.5")])]});
            var Q9;
            Q9=makeQuery(id+"F2.opExtrude","SWEPT_BODY",BODY,{"disambiguationData":[OSD([sQuery(id+"F0.wireOp",EDGE,"E1.1"),sQuery(id+"F0.wireOp",EDGE,"E1.2"),sQuery(id+"F0.wireOp",EDGE,"E12.2"),sQuery(id+"F0.wireOp",EDGE,"E12.3"),sQuery(id+"F0.wireOp",EDGE,"E25.2"),sQuery(id+"F0.wireOp",EDGE,"E25.3")])]});
            var Q10;
            Q10=makeQuery(id+"F2.opExtrude","SWEPT_BODY",BODY,{"disambiguationData":[OSD([sQuery(id+"F0.wireOp",EDGE,"E6.1"),sQuery(id+"F0.wireOp",EDGE,"E7.4"),sQuery(id+"F0.wireOp",EDGE,"E25.2")])]});
            var Q11;
            Q11=makeQuery(id+"F3.opExtrude","SWEPT_BODY",BODY,{"disambiguationData":[OSD([sQuery(id+"F0.wireOp",EDGE,"E1.5"),sQuery(id+"F0.wireOp",EDGE,"E2.1"),sQuery(id+"F0.wireOp",EDGE,"E10.1"),sQuery(id+"F0.wireOp",EDGE,"E25.0")])]});
            var Q12;
            Q12=makeQuery(id+"F1.opExtrude","SWEPT_BODY",BODY,{"disambiguationData":[OSD([sQuery(id+"F0.wireOp",EDGE,"E2.0"),sQuery(id+"F0.wireOp",EDGE,"E2.1"),sQuery(id+"F0.wireOp",EDGE,"E10.0"),sQuery(id+"F0.wireOp",EDGE,"E10.1"),sQuery(id+"F0.wireOp",EDGE,"E25.0"),sQuery(id+"F0.wireOp",EDGE,"E25.1")])]});
            var Q13;
            Q13=makeQuery(id+"F2.opExtrude","SWEPT_BODY",BODY,{"disambiguationData":[OSD([sQuery(id+"F0.wireOp",EDGE,"E2.1"),sQuery(id+"F0.wireOp",EDGE,"E3.0"),sQuery(id+"F0.wireOp",EDGE,"E25.0")])]});
            booleanBodies(context, id + "F5", {"operationType" : BooleanOperationType.UNION, "tools" : qUnion([Q0, Q1, Q2, Q3, Q4, Q5, Q6, Q7, Q8, Q9, Q10, Q11, Q12, Q13])});
        }
        {
            var Q0;
            Q0=makeQuery(id+"F2.opExtrude","SWEPT_BODY",BODY,{"disambiguationData":[OSD([sQuery(id+"F0.wireOp",EDGE,"E2.0"),sQuery(id+"F0.wireOp",EDGE,"E7.5"),sQuery(id+"F0.wireOp",EDGE,"E25.1")])]});
            var Q1;
            Q1=makeQuery(id+"F2.opExtrude","SWEPT_BODY",BODY,{"disambiguationData":[OSD([sQuery(id+"F0.wireOp",EDGE,"E1.0"),sQuery(id+"F0.wireOp",EDGE,"E1.1"),sQuery(id+"F0.wireOp",EDGE,"E11.1"),sQuery(id+"F0.wireOp",EDGE,"E11.2"),sQuery(id+"F0.wireOp",EDGE,"E25.1"),sQuery(id+"F0.wireOp",EDGE,"E25.2")])]});
            booleanBodies(context, id + "F6", {"operationType" : BooleanOperationType.UNION, "tools" : qUnion([Q0, Q1])});
        }
    });
